MODEL slx_26bd53d3a1b2
KIND model
CONFIG AbsTol = auto
CONFIG EnableMultiTasking = on
CONFIG FixedStep = auto
CONFIG MaxStep = auto
CONFIG MinStep = auto
CONFIG RelTol = 1e-3
CONFIG SampleTimeConstraint = Unconstrained
CONFIG SolverName = ode45
CONFIG StartTime = 0.0
CONFIG StopTime = 10.0
BLOCK [Reference] Band-Limited White Noise  REF=simulink/Sources/Band-Limited
White Noise
  NameLocation = right
  Ports = [0, 1]
  SourceBlock = simulink/Sources/Band-Limited\nWhite Noise
  SourceProductBaseCode = SL
  SourceType = Band-Limited White Noise.
BLOCK [Scope] Input
  Floating = off
  NameLocation = left
  NumInputPorts = 1
  Ports = [1]
  ScopeSpecificationString = C++SS(StrPVP('Location','[456, 165, 780, 404]'),StrPVP('Open','off'),MxPVP('AxesTitles',54,'struct(''axes1'',''%<SignalLabel>'')'),MxPVP('ScopeGraphics',57,'struct(''FigureColor'',''[0.156862745098039 0.156862745098039 0.156862745098039]'',''AxesColor'',''[0 0 0]'',''AxesTickColor'',''[0.686274509803922 0.686274509803922 0.686274509803922]'',''LineColors'',''[1 1 0;1 0 1;0 1 1;1 0 0;0 1 0;0 0 1]''...<+390ch>
BLOCK [Scope] Output
  Floating = off
  NumInputPorts = 1
  Ports = [1]
  ScopeSpecificationString = C++SS(StrPVP('Location','[893, 463, 1217, 702]'),StrPVP('Open','off'),MxPVP('AxesTitles',54,'struct(''axes1'',''%<SignalLabel>'')'),MxPVP('ScopeGraphics',57,'struct(''FigureColor'',''[0.156862745098039 0.156862745098039 0.156862745098039]'',''AxesColor'',''[0 0 0]'',''AxesTickColor'',''[0.686274509803922 0.686274509803922 0.686274509803922]'',''LineColors'',''[1 1 0;1 0 1;0 1 1;1 0 0;0 1 0;0 0 1]'...<+391ch>
BLOCK [Integrator] Process
  Ports = [1, 1]
BLOCK [Scope] Schedule
  Floating = off
  NumInputPorts = 1
  Ports = [1]
  ScopeSpecificationString = Simulink.scopes.TimeScopeBlockCfg('CurrentConfiguration', extmgr.ConfigurationSet(extmgr.Configuration('Core','General UI',true,'FigureColor',[0.156862745098039 0.156862745098039 0.156862745098039]),extmgr.Configuration('Core','Source UI',true),extmgr.Configuration('Sources','WiredSimulink',true,'DataLoggingSaveFormat','StructureWithTime','DataLoggingDecimation','1','DataLoggingDecimateData',true)...<+2700ch>
BLOCK [Sum] Sum
  InputSameDT = on
  Inputs = ++|
  OutDataTypeStr = Inherit: Same as first input
  Ports = [2, 1]
  SaturateOnIntegerOverflow = on
BLOCK [Reference] TrueTime Kernel  REF=truetime/TrueTime Kernel  (lib defined in slx_0362a698a4ec)
  Ports = [1, 2]
  SourceBlock = truetime/TrueTime Kernel
ANNOTATION (root): TrueTime 2.0 A Simple Example <copyright redacted>
LINE Band-Limited White Noise:1 -> Sum:1
NET Process:1 -> Output:1, TrueTime Kernel:1
LINE Sum:1 -> Process:1
NET TrueTime Kernel:1 -> Input:1, Sum:2
LINE TrueTime Kernel:2 -> Schedule:1
note: NET lines group one-source signal fan-out (src -> all destinations, sorted); 1:1 wires keep LINE
